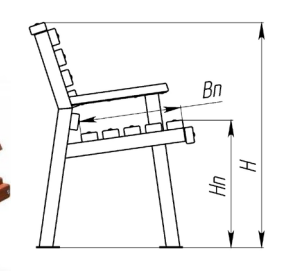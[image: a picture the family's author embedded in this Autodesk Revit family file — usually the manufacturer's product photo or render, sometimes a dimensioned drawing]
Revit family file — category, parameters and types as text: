
# Revit family: 6680 Комплект дачной мебели «Модерн» Хоббика
name_source: partatom
category: Антураж
revit_build: Autodesk Revit 2018 (Build: 20180423_1000(x64)
units: mm (PartAtom-declared; Revit-internal decimal feet)

## family parameters
Всегда вертикально = Да
Источник визуального образа = Геометрия семейства
На основе рабочей плоскости = Нет
Общий = Нет
При загрузке вырезать с полостями = Нет
Точка расчета площади = Нет

## types (2) — shared parameters
URL = https://hobbyka.ru
Артикул товара = Арт. 6680
Высота скамейки = 840 мм
Высота стола = 800 мм
Группа модели = Комплекты садовой мебели
Изготовитель = ООО «Хоббика»
Изображение типоразмера = Комплект дачной мебели «Модерн» Арт 6680.jpg
Материал изделия = Сталь, дерево
Цвет опор = Сталь
Цвет отделки = Дерево
Ширина скамейки = 600 мм
Ширина стола = 1100 мм
zero-valued in all types: Высота

## per-type parameters (varying)
| type | Версия 2,0 м | Версия 3,0 м | Длина | Описание |
| Версия 2,0 м | Да | Нет | 2000 мм | Комплект дачной мебели «Модерн». Версия 2,0 м |
| Версия 3,0 м | Нет | Да | 3000 мм | Комплект дачной мебели «Модерн». Версия 3,0 м |
